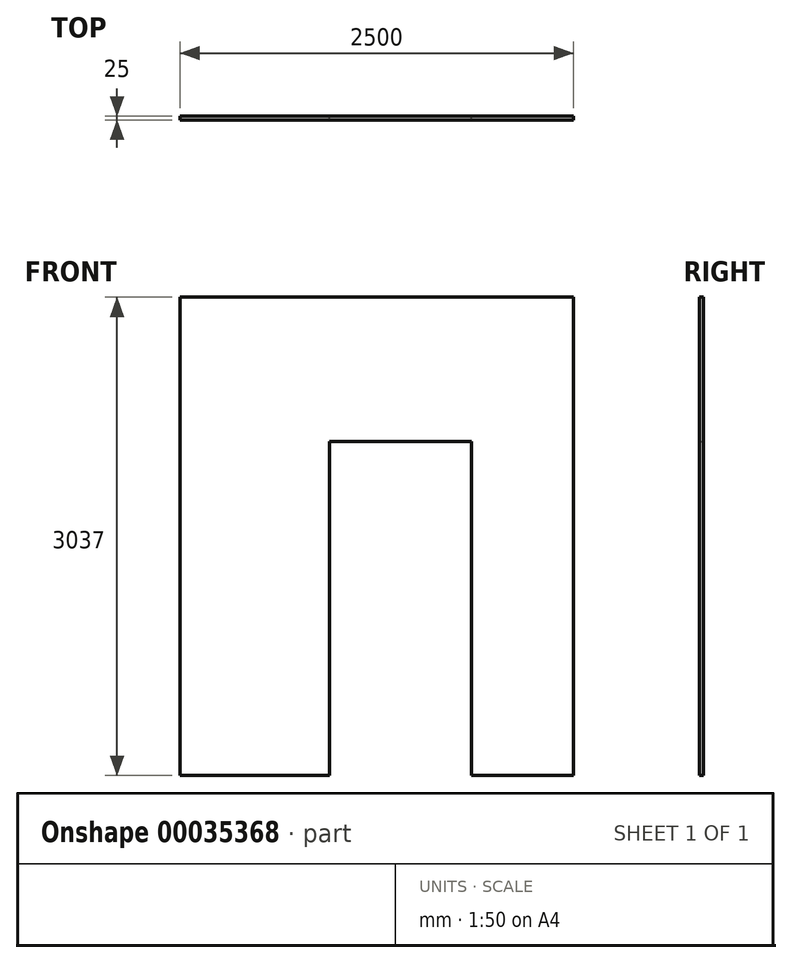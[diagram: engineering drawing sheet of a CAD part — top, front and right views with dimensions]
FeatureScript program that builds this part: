
annotation { "Feature Type Name" : "Feature", "Feature Type Description" : "" }
export const myFeature = defineFeature(function(context is Context, id is Id, definition is map)
    precondition{}
    {
        {
            var Q0;
            Q0=qCreatedBy(makeId("Front.planeOp"),FACE);
            var sketch = newSketch(context, id + "F0", { "sketchPlane" : qUnion([Q0])});
            skLineSegment(sketch, "E0.rect.bottom", {"start": v(1250, -1518.5) * mm, "end": v(600, -1518.5) * mm});
            skLineSegment(sketch, "E0.rect.top", {"start": v(1250, 1518.5) * mm, "end": v(-1250, 1518.5) * mm});
            skLineSegment(sketch, "E0.rect.left", {"start": v(1250, -1518.5) * mm, "end": v(1250, 1518.5) * mm});
            skLineSegment(sketch, "E0.rect.right", {"start": v(-1250, -1518.5) * mm, "end": v(-1250, 1518.5) * mm});
            skPoint(sketch, "E0.rect.middle", {"position": v(0, 0) * mm});
            skLineSegment(sketch, "E1", {"start": v(-300, -1518.5) * mm, "end": v(-1250, -1518.5) * mm});
            skLineSegment(sketch, "E2", {"start": v(-300, -1518.5) * mm, "end": v(-300, 603.5) * mm});
            skLineSegment(sketch, "E3", {"start": v(-300, 603.5) * mm, "end": v(600, 603.5) * mm});
            skLineSegment(sketch, "E4", {"start": v(600, 603.5) * mm, "end": v(600, -1518.5) * mm});
            skSolve(sketch);
        }
        {
            var Q0;
            Q0=makeQuery(id+"F0.imprint","IMPRINT",FACE,{"disambiguationData":[TD([[makeQuery(id+"F0.imprint","IMPRINT",EDGE,{"derivedFrom":sQuery(id+"F0.wireOp",EDGE,"E0.rect.bottom")}),-1.0]])]});
            extrude(context, id + "F1", {"entities" : qUnion([Q0]), "depth" : 25 * mm});
        }
    });
